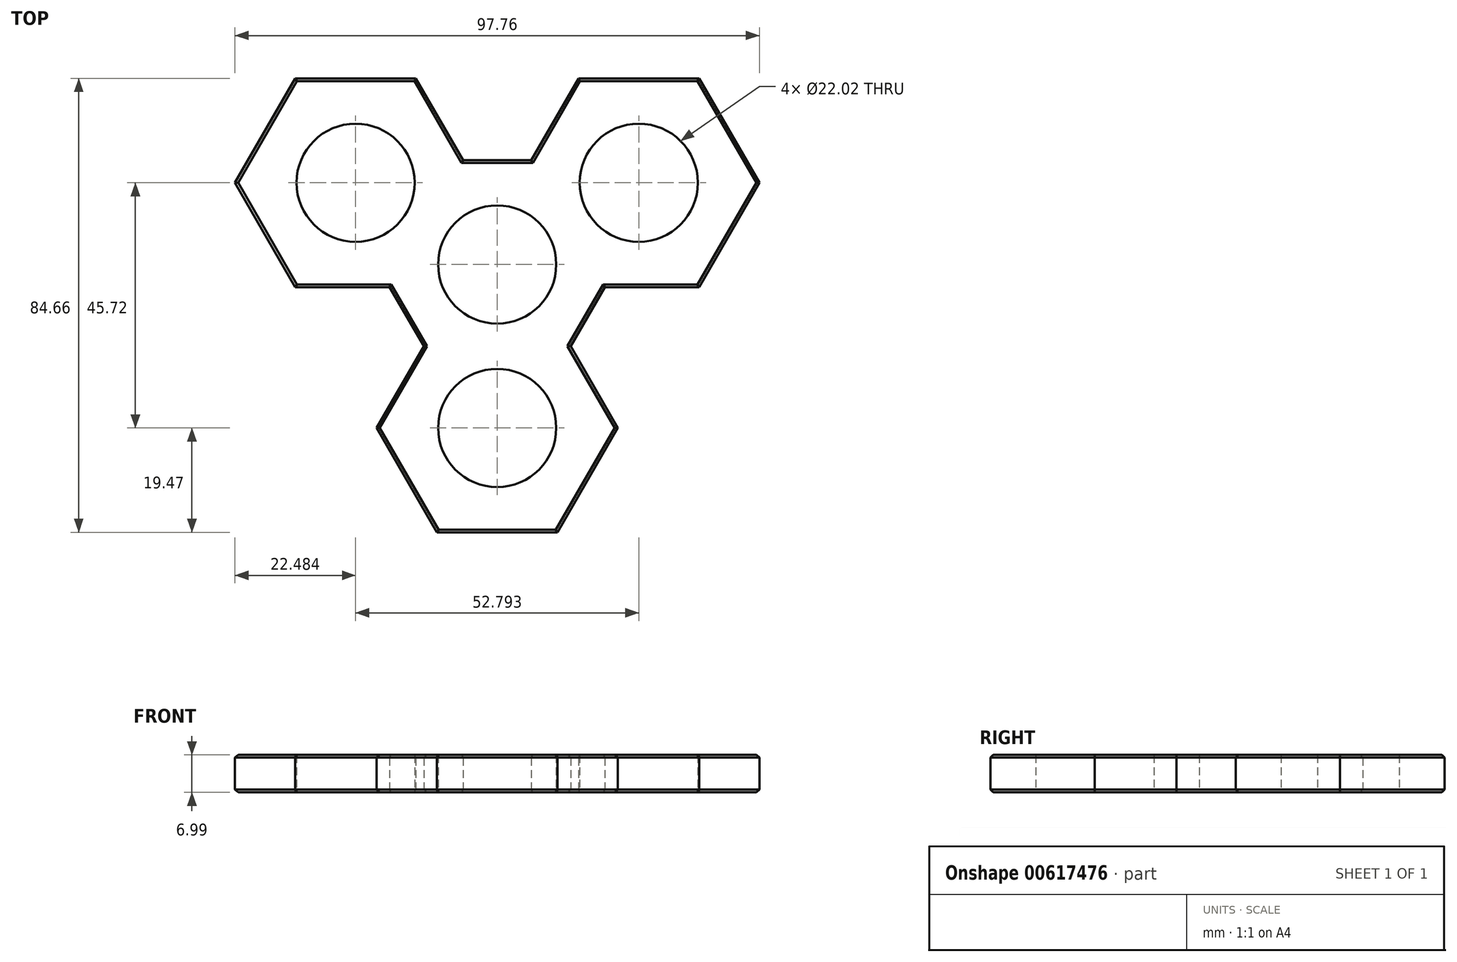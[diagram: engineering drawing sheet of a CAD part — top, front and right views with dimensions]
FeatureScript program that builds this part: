
annotation { "Feature Type Name" : "Feature", "Feature Type Description" : "" }
export const myFeature = defineFeature(function(context is Context, id is Id, definition is map)
    precondition{}
    {
        {
            var Q0;
            Q0=qCreatedBy(makeId("Top.planeOp"),FACE);
            var sketch = newSketch(context, id + "F0", { "sketchPlane" : qUnion([Q0])});
            skCircle(sketch, "E0", {"center": v(0, 0) * mm, "radius": 11.01 * mm});
            skLineSegment(sketch, "E1", {"start": v(0, 0) * mm, "end": v(0, -30.48) * mm});
            skLineSegment(sketch, "E2", {"start": v(0, -30.48) * mm, "end": v(0, 0) * mm});
            skLineSegment(sketch, "E3", {"start": v(0, 0) * mm, "end": v(-26.4, 15.24) * mm});
            skLineSegment(sketch, "E4", {"start": v(-26.4, 15.24) * mm, "end": v(0, 0) * mm});
            skLineSegment(sketch, "E5", {"start": v(0, 0) * mm, "end": v(26.4, 15.24) * mm});
            skCircle(sketch, "E6", {"center": v(-26.4, 15.24) * mm, "radius": 11.01 * mm});
            skCircle(sketch, "E7", {"center": v(0, -30.48) * mm, "radius": 11.01 * mm});
            skCircle(sketch, "E8", {"center": v(26.4, 15.24) * mm, "radius": 11.01 * mm});
            skCircle(sketch, "E9", {"center": v(-26.4, 15.24) * mm, "radius": 19.47 * mm});
            skCircle(sketch, "E10", {"center": v(0, 0) * mm, "radius": 19.47 * mm});
            skCircle(sketch, "E11", {"center": v(26.4, 15.24) * mm, "radius": 19.47 * mm});
            skCircle(sketch, "E12", {"center": v(0, -30.48) * mm, "radius": 19.47 * mm});
            skCircle(sketch, "E13.cCircle", {"center": v(0, 0) * mm, "radius": 19.47 * mm, "construction": true});
            skCircle(sketch, "E14.cCircle", {"center": v(-26.4, 15.24) * mm, "radius": 19.47 * mm, "construction": true});
            skCircle(sketch, "E15.cCircle", {"center": v(0, -30.48) * mm, "radius": 19.47 * mm, "construction": true});
            skLineSegment(sketch, "E16.0", {"start": v(-37.64, 34.7) * mm, "end": v(-15.16, 34.7) * mm});
            skLineSegment(sketch, "E16.1", {"start": v(-15.16, 34.7) * mm, "end": v(-3.92, 15.24) * mm});
            skLineSegment(sketch, "E16.2", {"start": v(-3.92, 15.24) * mm, "end": v(-15.16, -4.23) * mm});
            skLineSegment(sketch, "E16.3", {"start": v(-15.16, -4.23) * mm, "end": v(-37.64, -4.23) * mm});
            skLineSegment(sketch, "E16.4", {"start": v(-37.64, -4.23) * mm, "end": v(-48.88, 15.24) * mm});
            skLineSegment(sketch, "E16.5", {"start": v(-48.88, 15.24) * mm, "end": v(-37.64, 34.7) * mm});
            skPoint(sketch, "E16.0.midPoint", {"position": v(-26.4, 34.7) * mm});
            skLineSegment(sketch, "E17.0", {"start": v(-11.24, 19.47) * mm, "end": v(11.24, 19.47) * mm});
            skLineSegment(sketch, "E17.1", {"start": v(11.24, 19.47) * mm, "end": v(22.48, 0) * mm});
            skLineSegment(sketch, "E17.2", {"start": v(22.48, 0) * mm, "end": v(11.24, -19.47) * mm});
            skLineSegment(sketch, "E17.3", {"start": v(11.24, -19.47) * mm, "end": v(-11.24, -19.47) * mm});
            skLineSegment(sketch, "E17.4", {"start": v(-11.24, -19.47) * mm, "end": v(-22.48, 0) * mm});
            skLineSegment(sketch, "E17.5", {"start": v(-22.48, 0) * mm, "end": v(-11.24, 19.47) * mm});
            skPoint(sketch, "E17.0.midPoint", {"position": v(0, 19.47) * mm});
            skCircle(sketch, "E18.cCircle", {"center": v(26.4, 15.24) * mm, "radius": 19.47 * mm, "construction": true});
            skLineSegment(sketch, "E18.0", {"start": v(15.16, 34.7) * mm, "end": v(37.64, 34.7) * mm});
            skLineSegment(sketch, "E18.1", {"start": v(37.64, 34.7) * mm, "end": v(48.88, 15.24) * mm});
            skLineSegment(sketch, "E18.2", {"start": v(48.88, 15.24) * mm, "end": v(37.64, -4.23) * mm});
            skLineSegment(sketch, "E18.3", {"start": v(37.64, -4.23) * mm, "end": v(15.16, -4.23) * mm});
            skLineSegment(sketch, "E18.4", {"start": v(15.16, -4.23) * mm, "end": v(3.92, 15.24) * mm});
            skLineSegment(sketch, "E18.5", {"start": v(3.92, 15.24) * mm, "end": v(15.16, 34.7) * mm});
            skPoint(sketch, "E18.0.midPoint", {"position": v(26.4, 34.7) * mm});
            skLineSegment(sketch, "E19.0", {"start": v(-11.24, -11.01) * mm, "end": v(11.24, -11.01) * mm});
            skLineSegment(sketch, "E19.1", {"start": v(11.24, -11.01) * mm, "end": v(22.48, -30.48) * mm});
            skLineSegment(sketch, "E19.2", {"start": v(22.48, -30.48) * mm, "end": v(11.24, -49.95) * mm});
            skLineSegment(sketch, "E19.3", {"start": v(11.24, -49.95) * mm, "end": v(-11.24, -49.95) * mm});
            skLineSegment(sketch, "E19.4", {"start": v(-11.24, -49.95) * mm, "end": v(-22.48, -30.48) * mm});
            skLineSegment(sketch, "E19.5", {"start": v(-22.48, -30.48) * mm, "end": v(-11.24, -11.01) * mm});
            skPoint(sketch, "E19.0.midPoint", {"position": v(0, -11.01) * mm});
            skSolve(sketch);
        }
        {
            var Q0;
            Q0 = qSketchRegion(id + "F0", true);
            var Q1;
            {var subQ0=sQuery(id+"F0.wireOp",EDGE,"E10");var subQ3=sQuery(id+"F0.wireOp",EDGE,"E12");var subQ5=makeQuery(id+"F0.imprint","INTERSECT",VERTEX,{"disambiguationData":[OD(1.0)],"derivedFrom":[subQ0,subQ3]});Q1=makeQuery(id+"F0.imprint","IMPRINT",FACE,{"disambiguationData":[TD([[makeQuery(id+"F0.imprint","IMPRINT",EDGE,{"disambiguationData":[TD([[subQ5,1.0]])],"derivedFrom":subQ0}),1.0]])]});}
            var Q2;
            {var subQ0=sQuery(id+"F0.wireOp",EDGE,"E12");var subQ1=sQuery(id+"F0.wireOp",EDGE,"E10");var subQ2=makeQuery(id+"F0.imprint","INTERSECT",VERTEX,{"disambiguationData":[OD(1.0)],"derivedFrom":[subQ1,subQ0]});Q2=makeQuery(id+"F0.imprint","IMPRINT",FACE,{"disambiguationData":[TD([[makeQuery(id+"F0.imprint","IMPRINT",EDGE,{"disambiguationData":[TD([[subQ2,-1.0]])],"derivedFrom":subQ1}),1.0]])]});}
            var Q3;
            {var subQ0=sQuery(id+"F0.wireOp",EDGE,"E12");var subQ1=sQuery(id+"F0.wireOp",EDGE,"E10");var subQ2=makeQuery(id+"F0.imprint","INTERSECT",VERTEX,{"disambiguationData":[OD(1.0)],"derivedFrom":[subQ1,subQ0]});Q3=makeQuery(id+"F0.imprint","IMPRINT",FACE,{"disambiguationData":[TD([[makeQuery(id+"F0.imprint","IMPRINT",EDGE,{"disambiguationData":[TD([[subQ2,1.0]])],"derivedFrom":subQ0}),1.0]])]});}
            var Q4;
            {var subQ0=sQuery(id+"F0.wireOp",EDGE,"E10");var subQ3=sQuery(id+"F0.wireOp",EDGE,"E12");var subQ5=makeQuery(id+"F0.imprint","INTERSECT",VERTEX,{"disambiguationData":[OD(0.0)],"derivedFrom":[subQ0,subQ3]});Q4=makeQuery(id+"F0.imprint","IMPRINT",FACE,{"disambiguationData":[TD([[makeQuery(id+"F0.imprint","IMPRINT",EDGE,{"disambiguationData":[TD([[subQ5,-1.0]])],"derivedFrom":subQ0}),1.0]])]});}
            var Q5;
            {var subQ0=sQuery(id+"F0.wireOp",EDGE,"E12");var subQ1=sQuery(id+"F0.wireOp",EDGE,"E10");var subQ2=makeQuery(id+"F0.imprint","INTERSECT",VERTEX,{"disambiguationData":[OD(0.0)],"derivedFrom":[subQ1,subQ0]});Q5=makeQuery(id+"F0.imprint","IMPRINT",FACE,{"disambiguationData":[TD([[makeQuery(id+"F0.imprint","IMPRINT",EDGE,{"disambiguationData":[TD([[subQ2,-1.0]])],"derivedFrom":subQ0}),1.0]])]});}
            var Q6;
            {var subQ0=sQuery(id+"F0.wireOp",EDGE,"E19.5");var subQ1=sQuery(id+"F0.wireOp",EDGE,"E10");var subQ2=makeQuery(id+"F0.imprint","INTERSECT",VERTEX,{"derivedFrom":[subQ1,subQ0]});Q6=makeQuery(id+"F0.imprint","IMPRINT",FACE,{"disambiguationData":[TD([[makeQuery(id+"F0.imprint","IMPRINT",EDGE,{"disambiguationData":[TD([[subQ2,-1.0]])],"derivedFrom":subQ1}),1.0]])]});}
            var Q7;
            {var subQ0=sQuery(id+"F0.wireOp",EDGE,"E10");var subQ3=sQuery(id+"F0.wireOp",EDGE,"E11");var subQ5=makeQuery(id+"F0.imprint","INTERSECT",VERTEX,{"disambiguationData":[OD(1.0)],"derivedFrom":[subQ0,subQ3]});Q7=makeQuery(id+"F0.imprint","IMPRINT",FACE,{"disambiguationData":[TD([[makeQuery(id+"F0.imprint","IMPRINT",EDGE,{"disambiguationData":[TD([[subQ5,-1.0]])],"derivedFrom":subQ0}),1.0]])]});}
            var Q8;
            {var subQ0=sQuery(id+"F0.wireOp",EDGE,"E10");var subQ3=sQuery(id+"F0.wireOp",EDGE,"E11");var subQ5=makeQuery(id+"F0.imprint","INTERSECT",VERTEX,{"disambiguationData":[OD(0.0)],"derivedFrom":[subQ0,subQ3]});Q8=makeQuery(id+"F0.imprint","IMPRINT",FACE,{"disambiguationData":[TD([[makeQuery(id+"F0.imprint","IMPRINT",EDGE,{"disambiguationData":[TD([[subQ5,1.0]])],"derivedFrom":subQ0}),1.0]])]});}
            var Q9;
            {var subQ0=sQuery(id+"F0.wireOp",EDGE,"E11");var subQ1=sQuery(id+"F0.wireOp",EDGE,"E10");var subQ2=makeQuery(id+"F0.imprint","INTERSECT",VERTEX,{"disambiguationData":[OD(0.0)],"derivedFrom":[subQ1,subQ0]});Q9=makeQuery(id+"F0.imprint","IMPRINT",FACE,{"disambiguationData":[TD([[makeQuery(id+"F0.imprint","IMPRINT",EDGE,{"disambiguationData":[TD([[subQ2,1.0]])],"derivedFrom":subQ0}),1.0]])]});}
            var Q10;
            {var subQ0=sQuery(id+"F0.wireOp",EDGE,"E10");var subQ3=sQuery(id+"F0.wireOp",EDGE,"E9");var subQ5=makeQuery(id+"F0.imprint","INTERSECT",VERTEX,{"disambiguationData":[OD(0.0)],"derivedFrom":[subQ3,subQ0]});Q10=makeQuery(id+"F0.imprint","IMPRINT",FACE,{"disambiguationData":[TD([[makeQuery(id+"F0.imprint","IMPRINT",EDGE,{"disambiguationData":[TD([[subQ5,1.0]])],"derivedFrom":subQ3}),1.0]])]});}
            var Q11;
            {var subQ0=sQuery(id+"F0.wireOp",EDGE,"E17.0");var subQ1=sQuery(id+"F0.wireOp",EDGE,"E9");var subQ2=makeQuery(id+"F0.imprint","INTERSECT",VERTEX,{"derivedFrom":[subQ1,subQ0]});Q11=makeQuery(id+"F0.imprint","IMPRINT",FACE,{"disambiguationData":[TD([[makeQuery(id+"F0.imprint","IMPRINT",EDGE,{"disambiguationData":[TD([[subQ2,1.0]])],"derivedFrom":subQ1}),1.0]])]});}
            var Q12;
            {var subQ0=sQuery(id+"F0.wireOp",EDGE,"E10");var subQ1=sQuery(id+"F0.wireOp",EDGE,"E9");var subQ2=makeQuery(id+"F0.imprint","INTERSECT",VERTEX,{"disambiguationData":[OD(0.0)],"derivedFrom":[subQ1,subQ0]});Q12=makeQuery(id+"F0.imprint","IMPRINT",FACE,{"disambiguationData":[TD([[makeQuery(id+"F0.imprint","IMPRINT",EDGE,{"disambiguationData":[TD([[subQ2,1.0]])],"derivedFrom":subQ0}),1.0]])]});}
            var Q13;
            {var subQ0=sQuery(id+"F0.wireOp",EDGE,"E17.4");var subQ1=sQuery(id+"F0.wireOp",EDGE,"E9");var subQ2=makeQuery(id+"F0.imprint","INTERSECT",VERTEX,{"derivedFrom":[subQ1,subQ0]});Q13=makeQuery(id+"F0.imprint","IMPRINT",FACE,{"disambiguationData":[TD([[makeQuery(id+"F0.imprint","IMPRINT",EDGE,{"disambiguationData":[TD([[subQ2,-1.0]])],"derivedFrom":subQ1}),1.0]])]});}
            var Q14;
            {var subQ0=sQuery(id+"F0.wireOp",EDGE,"E10");var subQ1=sQuery(id+"F0.wireOp",EDGE,"E9");var subQ2=makeQuery(id+"F0.imprint","INTERSECT",VERTEX,{"disambiguationData":[OD(1.0)],"derivedFrom":[subQ1,subQ0]});Q14=makeQuery(id+"F0.imprint","IMPRINT",FACE,{"disambiguationData":[TD([[makeQuery(id+"F0.imprint","IMPRINT",EDGE,{"disambiguationData":[TD([[subQ2,-1.0]])],"derivedFrom":subQ0}),1.0]])]});}
            var Q15;
            {var subQ0=sQuery(id+"F0.wireOp",EDGE,"E11");var subQ1=sQuery(id+"F0.wireOp",EDGE,"E10");var subQ2=makeQuery(id+"F0.imprint","INTERSECT",VERTEX,{"disambiguationData":[OD(0.0)],"derivedFrom":[subQ1,subQ0]});Q15=makeQuery(id+"F0.imprint","IMPRINT",FACE,{"disambiguationData":[TD([[makeQuery(id+"F0.imprint","IMPRINT",EDGE,{"disambiguationData":[TD([[subQ2,-1.0]])],"derivedFrom":subQ1}),1.0]])]});}
            var Q16;
            {var subQ0=sQuery(id+"F0.wireOp",EDGE,"E10");var subQ3=sQuery(id+"F0.wireOp",EDGE,"E9");var subQ5=makeQuery(id+"F0.imprint","INTERSECT",VERTEX,{"disambiguationData":[OD(1.0)],"derivedFrom":[subQ3,subQ0]});Q16=makeQuery(id+"F0.imprint","IMPRINT",FACE,{"disambiguationData":[TD([[makeQuery(id+"F0.imprint","IMPRINT",EDGE,{"disambiguationData":[TD([[subQ5,-1.0]])],"derivedFrom":subQ3}),1.0]])]});}
            var Q17;
            {var subQ0=sQuery(id+"F0.wireOp",EDGE,"E18.3");var subQ1=sQuery(id+"F0.wireOp",EDGE,"E10");var subQ2=makeQuery(id+"F0.imprint","INTERSECT",VERTEX,{"derivedFrom":[subQ1,subQ0]});Q17=makeQuery(id+"F0.imprint","IMPRINT",FACE,{"disambiguationData":[TD([[makeQuery(id+"F0.imprint","IMPRINT",EDGE,{"disambiguationData":[TD([[subQ2,-1.0]])],"derivedFrom":subQ1}),1.0]])]});}
            var Q18;
            {var subQ0=sQuery(id+"F0.wireOp",EDGE,"E11");var subQ1=sQuery(id+"F0.wireOp",EDGE,"E10");var subQ2=makeQuery(id+"F0.imprint","INTERSECT",VERTEX,{"disambiguationData":[OD(1.0)],"derivedFrom":[subQ1,subQ0]});Q18=makeQuery(id+"F0.imprint","IMPRINT",FACE,{"disambiguationData":[TD([[makeQuery(id+"F0.imprint","IMPRINT",EDGE,{"disambiguationData":[TD([[subQ2,-1.0]])],"derivedFrom":subQ0}),1.0]])]});}
            extrude(context, id + "F1", {"entities" : qUnion([Q0, Q1, Q2, Q3, Q4, Q5, Q6, Q7, Q8, Q9, Q10, Q11, Q12, Q13, Q14, Q15, Q16, Q17, Q18]), "depth" : 7 * mm, "offsetDistance" : 25.4 * mm});
        }
        {
            var Q0;
            Q0=makeQuery(id+"F1.opExtrude","CAP_EDGE",EDGE,{"disambiguationData":[OSD([sQuery(id+"F0.wireOp",EDGE,"E16.5")])],"isStart":false});
            var Q1;
            Q1=makeQuery(id+"F1.opExtrude","CAP_EDGE",EDGE,{"disambiguationData":[OSD([sQuery(id+"F0.wireOp",EDGE,"E16.0")])],"isStart":false});
            var Q2;
            Q2=makeQuery(id+"F1.opExtrude","CAP_EDGE",EDGE,{"disambiguationData":[OSD([sQuery(id+"F0.wireOp",EDGE,"E16.1")])],"isStart":false});
            var Q3;
            Q3=makeQuery(id+"F1.opExtrude","CAP_EDGE",EDGE,{"disambiguationData":[OSD([sQuery(id+"F0.wireOp",EDGE,"E17.0")])],"isStart":false});
            var Q4;
            Q4=makeQuery(id+"F1.opExtrude","CAP_EDGE",EDGE,{"disambiguationData":[OSD([sQuery(id+"F0.wireOp",EDGE,"E18.5")])],"isStart":false});
            var Q5;
            Q5=makeQuery(id+"F1.opExtrude","CAP_EDGE",EDGE,{"disambiguationData":[OSD([sQuery(id+"F0.wireOp",EDGE,"E18.0")])],"isStart":false});
            var Q6;
            Q6=makeQuery(id+"F1.opExtrude","CAP_EDGE",EDGE,{"disambiguationData":[OSD([sQuery(id+"F0.wireOp",EDGE,"E18.1")])],"isStart":false});
            var Q7;
            Q7=makeQuery(id+"F1.opExtrude","CAP_EDGE",EDGE,{"disambiguationData":[OSD([sQuery(id+"F0.wireOp",EDGE,"E18.2")])],"isStart":false});
            var Q8;
            Q8=makeQuery(id+"F1.opExtrude","CAP_EDGE",EDGE,{"disambiguationData":[OSD([sQuery(id+"F0.wireOp",EDGE,"E18.3")])],"isStart":false});
            var Q9;
            Q9=makeQuery(id+"F1.opExtrude","CAP_EDGE",EDGE,{"disambiguationData":[OSD([sQuery(id+"F0.wireOp",EDGE,"E17.2")])],"isStart":false});
            var Q10;
            Q10=makeQuery(id+"F1.opExtrude","CAP_EDGE",EDGE,{"disambiguationData":[OSD([sQuery(id+"F0.wireOp",EDGE,"E19.1")])],"isStart":false});
            var Q11;
            Q11=makeQuery(id+"F1.opExtrude","CAP_EDGE",EDGE,{"disambiguationData":[OSD([sQuery(id+"F0.wireOp",EDGE,"E19.2")])],"isStart":false});
            var Q12;
            Q12=makeQuery(id+"F1.opExtrude","CAP_EDGE",EDGE,{"disambiguationData":[OSD([sQuery(id+"F0.wireOp",EDGE,"E19.3")])],"isStart":false});
            var Q13;
            Q13=makeQuery(id+"F1.opExtrude","CAP_EDGE",EDGE,{"disambiguationData":[OSD([sQuery(id+"F0.wireOp",EDGE,"E19.4")])],"isStart":false});
            var Q14;
            Q14=makeQuery(id+"F1.opExtrude","CAP_EDGE",EDGE,{"disambiguationData":[OSD([sQuery(id+"F0.wireOp",EDGE,"E19.5")])],"isStart":false});
            var Q15;
            Q15=makeQuery(id+"F1.opExtrude","CAP_EDGE",EDGE,{"disambiguationData":[OSD([sQuery(id+"F0.wireOp",EDGE,"E17.4")])],"isStart":false});
            var Q16;
            Q16=makeQuery(id+"F1.opExtrude","CAP_EDGE",EDGE,{"disambiguationData":[OSD([sQuery(id+"F0.wireOp",EDGE,"E16.3")])],"isStart":false});
            var Q17;
            Q17=makeQuery(id+"F1.opExtrude","CAP_EDGE",EDGE,{"disambiguationData":[OSD([sQuery(id+"F0.wireOp",EDGE,"E16.4")])],"isStart":false});
            var Q18;
            Q18=makeQuery(id+"F1.opExtrude","CAP_EDGE",EDGE,{"disambiguationData":[OSD([sQuery(id+"F0.wireOp",EDGE,"E18.1")])],"isStart":true});
            var Q19;
            Q19=makeQuery(id+"F1.opExtrude","CAP_EDGE",EDGE,{"disambiguationData":[OSD([sQuery(id+"F0.wireOp",EDGE,"E18.0")])],"isStart":true});
            var Q20;
            Q20=makeQuery(id+"F1.opExtrude","CAP_EDGE",EDGE,{"disambiguationData":[OSD([sQuery(id+"F0.wireOp",EDGE,"E18.5")])],"isStart":true});
            var Q21;
            Q21=makeQuery(id+"F1.opExtrude","CAP_EDGE",EDGE,{"disambiguationData":[OSD([sQuery(id+"F0.wireOp",EDGE,"E17.0")])],"isStart":true});
            var Q22;
            Q22=makeQuery(id+"F1.opExtrude","CAP_EDGE",EDGE,{"disambiguationData":[OSD([sQuery(id+"F0.wireOp",EDGE,"E18.2")])],"isStart":true});
            var Q23;
            Q23=makeQuery(id+"F1.opExtrude","CAP_EDGE",EDGE,{"disambiguationData":[OSD([sQuery(id+"F0.wireOp",EDGE,"E18.3")])],"isStart":true});
            var Q24;
            Q24=makeQuery(id+"F1.opExtrude","CAP_EDGE",EDGE,{"disambiguationData":[OSD([sQuery(id+"F0.wireOp",EDGE,"E17.2")])],"isStart":true});
            var Q25;
            Q25=makeQuery(id+"F1.opExtrude","CAP_EDGE",EDGE,{"disambiguationData":[OSD([sQuery(id+"F0.wireOp",EDGE,"E19.1")])],"isStart":true});
            var Q26;
            Q26=makeQuery(id+"F1.opExtrude","CAP_EDGE",EDGE,{"disambiguationData":[OSD([sQuery(id+"F0.wireOp",EDGE,"E19.2")])],"isStart":true});
            var Q27;
            Q27=makeQuery(id+"F1.opExtrude","CAP_EDGE",EDGE,{"disambiguationData":[OSD([sQuery(id+"F0.wireOp",EDGE,"E19.3")])],"isStart":true});
            var Q28;
            Q28=makeQuery(id+"F1.opExtrude","CAP_EDGE",EDGE,{"disambiguationData":[OSD([sQuery(id+"F0.wireOp",EDGE,"E19.4")])],"isStart":true});
            var Q29;
            Q29=makeQuery(id+"F1.opExtrude","CAP_EDGE",EDGE,{"disambiguationData":[OSD([sQuery(id+"F0.wireOp",EDGE,"E19.5")])],"isStart":true});
            var Q30;
            Q30=makeQuery(id+"F1.opExtrude","CAP_EDGE",EDGE,{"disambiguationData":[OSD([sQuery(id+"F0.wireOp",EDGE,"E17.4")])],"isStart":true});
            var Q31;
            Q31=makeQuery(id+"F1.opExtrude","CAP_EDGE",EDGE,{"disambiguationData":[OSD([sQuery(id+"F0.wireOp",EDGE,"E16.3")])],"isStart":true});
            var Q32;
            Q32=makeQuery(id+"F1.opExtrude","CAP_EDGE",EDGE,{"disambiguationData":[OSD([sQuery(id+"F0.wireOp",EDGE,"E16.4")])],"isStart":true});
            var Q33;
            Q33=makeQuery(id+"F1.opExtrude","CAP_EDGE",EDGE,{"disambiguationData":[OSD([sQuery(id+"F0.wireOp",EDGE,"E16.5")])],"isStart":true});
            var Q34;
            Q34=makeQuery(id+"F1.opExtrude","CAP_EDGE",EDGE,{"disambiguationData":[OSD([sQuery(id+"F0.wireOp",EDGE,"E16.0")])],"isStart":true});
            var Q35;
            Q35=makeQuery(id+"F1.opExtrude","CAP_EDGE",EDGE,{"disambiguationData":[OSD([sQuery(id+"F0.wireOp",EDGE,"E16.1")])],"isStart":true});
            chamfer(context, id + "F2", {"entities" : qUnion([Q0, Q1, Q2, Q3, Q4, Q5, Q6, Q7, Q8, Q9, Q10, Q11, Q12, Q13, Q14, Q15, Q16, Q17, Q18, Q19, Q20, Q21, Q22, Q23, Q24, Q25, Q26, Q27, Q28, Q29, Q30, Q31, Q32, Q33, Q34, Q35]), "width" : 0.5 * mm, "tangentPropagation" : true});
        }
    });
